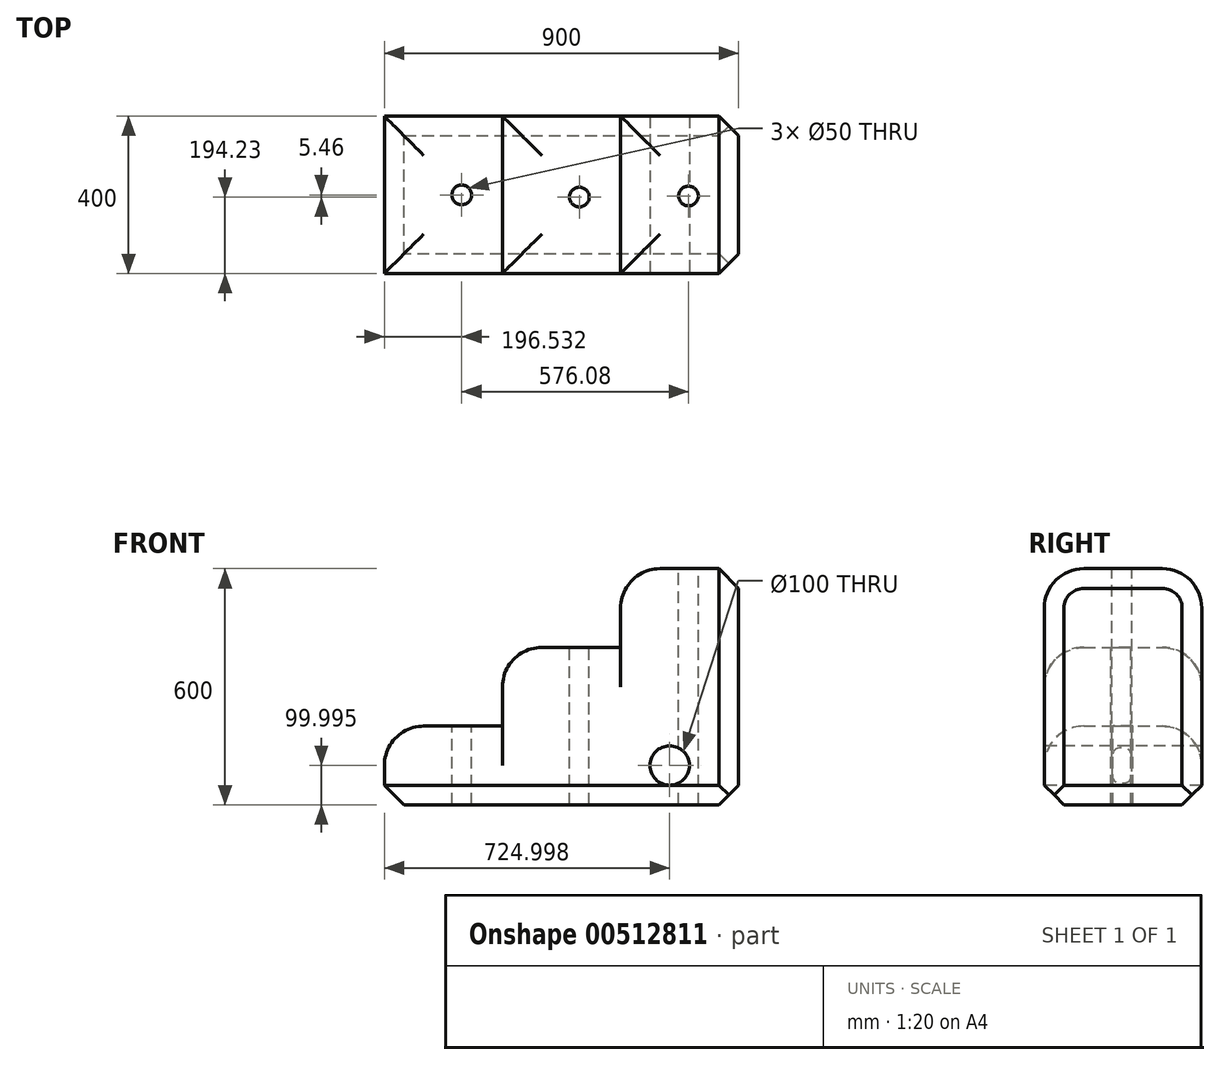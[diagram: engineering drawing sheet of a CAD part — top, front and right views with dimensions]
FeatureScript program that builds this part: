
annotation { "Feature Type Name" : "Feature", "Feature Type Description" : "" }
export const myFeature = defineFeature(function(context is Context, id is Id, definition is map)
    precondition{}
    {
        {
            var Q0;
            Q0=qCreatedBy(makeId("Front.planeOp"),FACE);
            var sketch = newSketch(context, id + "F0", { "sketchPlane" : qUnion([Q0])});
            skLineSegment(sketch, "E0", {"start": v(-480.11, -100.13) * mm, "end": v(-480.11, 99.87) * mm});
            skLineSegment(sketch, "E1", {"start": v(-480.11, 99.87) * mm, "end": v(-180.11, 99.87) * mm});
            skLineSegment(sketch, "E2", {"start": v(-180.11, 99.87) * mm, "end": v(-180.11, 299.87) * mm});
            skLineSegment(sketch, "E3", {"start": v(-180.11, 299.87) * mm, "end": v(119.89, 299.87) * mm});
            skLineSegment(sketch, "E4", {"start": v(119.89, 299.87) * mm, "end": v(119.89, 499.87) * mm});
            skLineSegment(sketch, "E5", {"start": v(419.89, 499.87) * mm, "end": v(419.89, -100.13) * mm});
            skLineSegment(sketch, "E6", {"start": v(419.89, -100.13) * mm, "end": v(-480.11, -100.13) * mm});
            skLineSegment(sketch, "E7", {"start": v(119.89, 499.87) * mm, "end": v(419.89, 499.87) * mm});
            skSolve(sketch);
        }
        {
            var Q0;
            Q0 = qSketchRegion(id + "F0", true);
            extrude(context, id + "F1", {"entities" : qUnion([Q0]), "depth" : 400 * mm});
        }
        {
            var Q0;
            Q0=makeQuery(id+"F1.opExtrude","CAP_EDGE",EDGE,{"disambiguationData":[OSD([sQuery(id+"F0.wireOp",EDGE,"E1")])],"isStart":true});
            var Q1;
            Q1=makeQuery(id+"F1.opExtrude","CAP_EDGE",EDGE,{"disambiguationData":[OSD([sQuery(id+"F0.wireOp",EDGE,"E1")])],"isStart":false});
            var Q2;
            Q2=makeQuery(id+"F1.opExtrude","SWEPT_EDGE",EDGE,{"disambiguationData":[OSD([sQuery(id+"F0.wireOp",EDGE,"E0"),sQuery(id+"F0.wireOp",EDGE,"E1")])]});
            fillet(context, id + "F2", {"entities" : qUnion([Q0, Q1, Q2]), "radius" : 100 * mm, "tangentPropagation" : true, "allowEdgeOverflow" : false});
        }
        {
            var Q0;
            Q0=makeQuery(id+"F1.opExtrude","CAP_EDGE",EDGE,{"disambiguationData":[OSD([sQuery(id+"F0.wireOp",EDGE,"E3")])],"isStart":true});
            var Q1;
            Q1=makeQuery(id+"F1.opExtrude","SWEPT_EDGE",EDGE,{"disambiguationData":[OSD([sQuery(id+"F0.wireOp",EDGE,"E2"),sQuery(id+"F0.wireOp",EDGE,"E3")])]});
            var Q2;
            Q2=makeQuery(id+"F1.opExtrude","CAP_EDGE",EDGE,{"disambiguationData":[OSD([sQuery(id+"F0.wireOp",EDGE,"E3")])],"isStart":false});
            fillet(context, id + "F3", {"entities" : qUnion([Q0, Q1, Q2]), "radius" : 100 * mm, "tangentPropagation" : true, "allowEdgeOverflow" : false});
        }
        {
            var Q0;
            Q0=makeQuery(id+"F1.opExtrude","CAP_EDGE",EDGE,{"disambiguationData":[OSD([sQuery(id+"F0.wireOp",EDGE,"E7")])],"isStart":true});
            var Q1;
            Q1=makeQuery(id+"F1.opExtrude","SWEPT_EDGE",EDGE,{"disambiguationData":[OSD([sQuery(id+"F0.wireOp",EDGE,"E4"),sQuery(id+"F0.wireOp",EDGE,"E7")])]});
            var Q2;
            Q2=makeQuery(id+"F1.opExtrude","CAP_EDGE",EDGE,{"disambiguationData":[OSD([sQuery(id+"F0.wireOp",EDGE,"E7")])],"isStart":false});
            fillet(context, id + "F4", {"entities" : qUnion([Q0, Q1, Q2]), "radius" : 100 * mm, "tangentPropagation" : true, "allowEdgeOverflow" : false});
        }
        {
            var Q0;
            Q0=makeQuery(id+"F1.opExtrude","CAP_EDGE",EDGE,{"disambiguationData":[OSD([sQuery(id+"F0.wireOp",EDGE,"E5")])],"isStart":false});
            var Q1;
            Q1=makeQuery(id+"F1.opExtrude","SWEPT_EDGE",EDGE,{"disambiguationData":[OSD([sQuery(id+"F0.wireOp",EDGE,"E5"),sQuery(id+"F0.wireOp",EDGE,"E6")])]});
            chamfer(context, id + "F5", {"entities" : qUnion([Q0, Q1]), "width" : 50 * mm, "tangentPropagation" : true});
        }
        {
            var Q0;
            Q0=makeQuery(id+"F1.opExtrude","CAP_EDGE",EDGE,{"disambiguationData":[OSD([sQuery(id+"F0.wireOp",EDGE,"E6")])],"isStart":false});
            var Q1;
            Q1=makeQuery(id+"F1.opExtrude","SWEPT_EDGE",EDGE,{"disambiguationData":[OSD([sQuery(id+"F0.wireOp",EDGE,"E0"),sQuery(id+"F0.wireOp",EDGE,"E6")])]});
            var Q2;
            Q2=makeQuery(id+"F1.opExtrude","CAP_EDGE",EDGE,{"disambiguationData":[OSD([sQuery(id+"F0.wireOp",EDGE,"E6")])],"isStart":true});
            chamfer(context, id + "F6", {"entities" : qUnion([Q0, Q1, Q2]), "width" : 50 * mm, "tangentPropagation" : true});
        }
        {
            var Q0;
            Q0=makeQuery(id+"F1.opExtrude","CAP_FACE",FACE,{"disambiguationData":[OSD([sQuery(id+"F0.wireOp",EDGE,"E0"),sQuery(id+"F0.wireOp",EDGE,"E1"),sQuery(id+"F0.wireOp",EDGE,"E2"),sQuery(id+"F0.wireOp",EDGE,"E3"),sQuery(id+"F0.wireOp",EDGE,"E4"),sQuery(id+"F0.wireOp",EDGE,"E5"),sQuery(id+"F0.wireOp",EDGE,"E6"),sQuery(id+"F0.wireOp",EDGE,"E7")])],"isStart":false});
            var sketch = newSketch(context, id + "F7", { "sketchPlane" : qUnion([Q0])});
            skCircle(sketch, "E8", {"center": v(244.89, -0.13) * mm, "radius": 50 * mm});
            skPoint(sketch, "E8.centerSnap0", {"position": v(244.89, 399.87) * mm});
            skSolve(sketch);
        }
        {
            var Q0;
            Q0 = qSketchRegion(id + "F7", true);
            extrude(context, id + "F8", {"entities" : qUnion([Q0]), "operationType" : NewBodyOperationType.ADD, "depth" : 25.4 * mm});
        }
        {
            var Q0;
            Q0=makeQuery(id+"F8.opExtrude","CAP_FACE",FACE,{"disambiguationData":[OSD([sQuery(id+"F7.wireOp",EDGE,"E8")])],"isStart":false});
            extrude(context, id + "F9", {"entities" : qUnion([Q0]), "operationType" : NewBodyOperationType.REMOVE, "endBound" : BoundingType.THROUGH_ALL, "oppositeDirection" : true, "depth" : 101.6 * mm});
        }
        {
            var Q0;
            Q0=makeQuery(id+"F1.opExtrude","SWEPT_FACE",FACE,{"disambiguationData":[OSD([sQuery(id+"F0.wireOp",EDGE,"E7")])]});
            var sketch = newSketch(context, id + "F10", { "sketchPlane" : qUnion([Q0])});
            skCircle(sketch, "E9", {"center": v(292.5, -203.04) * mm, "radius": 25 * mm});
            skCircle(sketch, "E10", {"center": v(15.38, -205.77) * mm, "radius": 25 * mm});
            skCircle(sketch, "E11", {"center": v(-283.58, -200.3) * mm, "radius": 25 * mm});
            skSolve(sketch);
        }
        {
            var Q0;
            Q0 = qSketchRegion(id + "F10", true);
            extrude(context, id + "F11", {"entities" : qUnion([Q0]), "operationType" : NewBodyOperationType.REMOVE, "endBound" : BoundingType.THROUGH_ALL, "oppositeDirection" : true, "depth" : 25.4 * mm});
        }
    });
